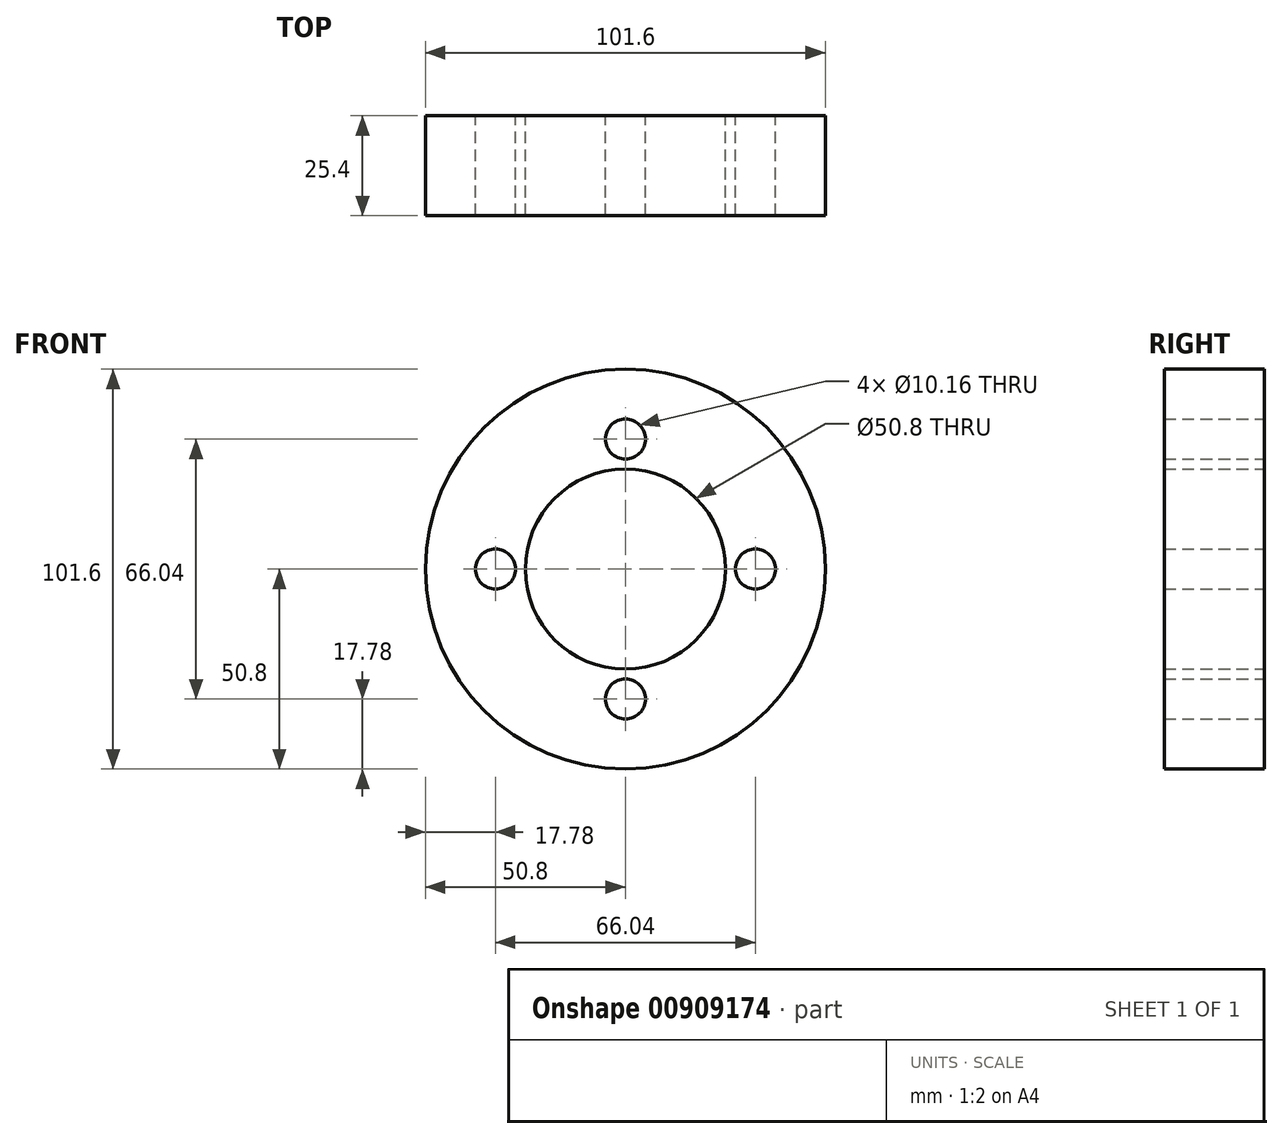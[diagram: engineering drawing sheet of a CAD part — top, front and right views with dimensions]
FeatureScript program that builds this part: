
annotation { "Feature Type Name" : "Feature", "Feature Type Description" : "" }
export const myFeature = defineFeature(function(context is Context, id is Id, definition is map)
    precondition{}
    {
        {
            var Q0;
            Q0=qCreatedBy(makeId("Front.planeOp"),FACE);
            var sketch = newSketch(context, id + "F0", { "sketchPlane" : qUnion([Q0])});
            skCircle(sketch, "E0", {"center": v(0, 0) * mm, "radius": 50.8 * mm});
            skCircle(sketch, "E1", {"center": v(0, 0) * mm, "radius": 25.4 * mm});
            skCircle(sketch, "E2", {"center": v(0, 33.02) * mm, "radius": 5.08 * mm});
            skCircle(sketch, "E3", {"center": v(33.02, 0) * mm, "radius": 5.08 * mm});
            skCircle(sketch, "E4", {"center": v(0, -33.02) * mm, "radius": 5.08 * mm});
            skCircle(sketch, "E5", {"center": v(-33.02, 0) * mm, "radius": 5.08 * mm});
            skSolve(sketch);
        }
        {
            var Q0;
            Q0=makeQuery(id+"F0.imprint","IMPRINT",FACE,{"disambiguationData":[TD([[makeQuery(id+"F0.imprint","IMPRINT",EDGE,{"derivedFrom":sQuery(id+"F0.wireOp",EDGE,"E0")}),1.0]])]});
            extrude(context, id + "F1", {"entities" : qUnion([Q0]), "depth" : 25.4 * mm, "offsetDistance" : 25.4 * mm});
        }
    });
